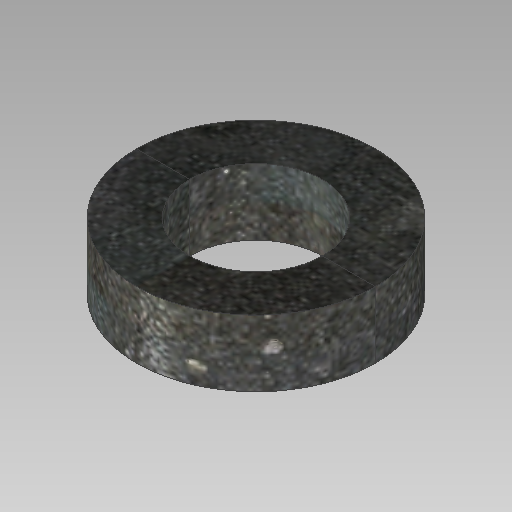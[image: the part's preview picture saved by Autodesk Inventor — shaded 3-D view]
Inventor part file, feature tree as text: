
AUTODESK INVENTOR PART (.ipt)
format: ipt  version: 2020.1 (Build 241239000, 239)  size: 257,024 bytes
history: native  units: mm
features: other x8, projected_geometry x2, extrude x1
ambient origin geometry x8: Origin, YZ Plane, XZ Plane, XY Plane, X Axis, Y Axis, Z Axis, Center Point
bodies: Solid1 (feature_tree)
feature tree (11):
  other  "Annotations"
  extrude  "Make Part"  Depth=54.0mm
  other  "Two Parts"
  other  "Tangent Plane"
  other  "Locate Hole Centres"
  other  "Two Piece Clamp Profile"
  projected_geometry  "Projected Loop1"
  projected_geometry  "Projected Loop2"
  other  "Part 1"
  other  "Part 2"
  other  "General Note 1"
